# Revit family: Deca_Ducha higiênica com registro e derivação_Wish_1984.WSH.ACT
name_source: partatom
category: Plumbing Fixtures
units: mm (PartAtom-declared; Revit-internal decimal feet)

## family parameters
Cut with Voids When Loaded = No
Host = Face
Part Type = Normal
Room Calculation Point = No
Round Connector Dimension = Use Radius
Shared = No

## types (2) — shared parameters
Aprovado por = quattroD
Atendimento ao Cliente = 0800-0117073
Categoria = Metais para banheiro
Composição Básica = Liga cobre (bronze e latão);Aço;Plástico de Engenharia;Elastômeros
Consumo = Otimização do jato de água
Criado por = quattroD
Código Pai = 1984.WSH.ACT
Default Elevation = 0.7 m
Diâmetro Água Fria = 0.02 m
Diâmetro Água Fria Saída = 0.02 m
Linha = Deca Wish
Manufacturer = DECA
Norma = NBR14877
Pressão máx. funcionamento = 40
Pressão mín. funcionamento = 2
Raio Água Fria = 0.01 m
Raio Água Fria Saída = 0.01 m
Segmento = Banheiro Luxo (D43)
Tipo de dispositivo economizador = Sim
Tipo de mecanismo utilizado = MVC -1/4 volta
Tipo de rosca de entrada = BSP NBR 8133
URL = www.deca.com.br
Vazão na Pressão máx. (L/min) = 6
Vazão na Pressão mín. (L/min) = 4

## per-type parameters (varying)
| type | Cor Principal | Cor Secundária | Material | Material Secundário | Model | Peso Líquido (Kg) |
| 1984.C.WSH.ACT.CR_Cromado | Cromado |  | Deca_Cromado | Deca_Cromado | 1984.C.WSH.ACT.CR | 0.913 |
| 1984.GL.WSH.ACT.RD_Red Gold | Red Gold | Branco | Deca_Red Gold | Deca_Branco | 1984.GL.WSH.ACT.RD | 0.95 |

## geometry (parser evidence)
native form markers: Sweep x1
no freeform markers — native parametric forms only
